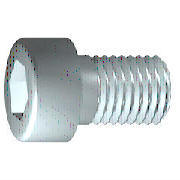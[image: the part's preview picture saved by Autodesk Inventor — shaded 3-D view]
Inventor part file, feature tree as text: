
AUTODESK INVENTOR PART (.ipt)
format: ipt  version: 2020 (Build 240168000, 168)  size: 196,096 bytes
history: native  units: mm (DEFAULTED — no unit token found)
features: sketch x2, extrude x1, plane x1, fillet x1
ambient origin geometry x7: Origin, YZ Plane, XY Plane, X Axis, Y Axis, Z Axis, Center Point
bodies: Solid1 (feature_tree), Body (feature_tree)
feature tree (5):
  extrude  "Slot"  Depth=2.8mm
  plane  "Work Plane1"
  fillet  "Fillet2"  Radius=2.8mm
  sketch  "Sketch1"  dims[d1=13.9mm d2=0.429515mm d3=2.8mm]
  sketch  "Sketch2"  dims[d4=2.3mm d5=60.0deg d6=4.0mm d7=4.0mm d8=2.886751mm d9=7.0mm d10=90.0deg d11=10.0mm d12=0.0mm d13=13.9mm d14=0.0mm d15=0.429415mm d16=0.429415mm d17=0.4mm d19=0.0mm d26=16.0mm d27=45.0deg d28=0.0mm d29=0.0mm d30=0.1mm]
